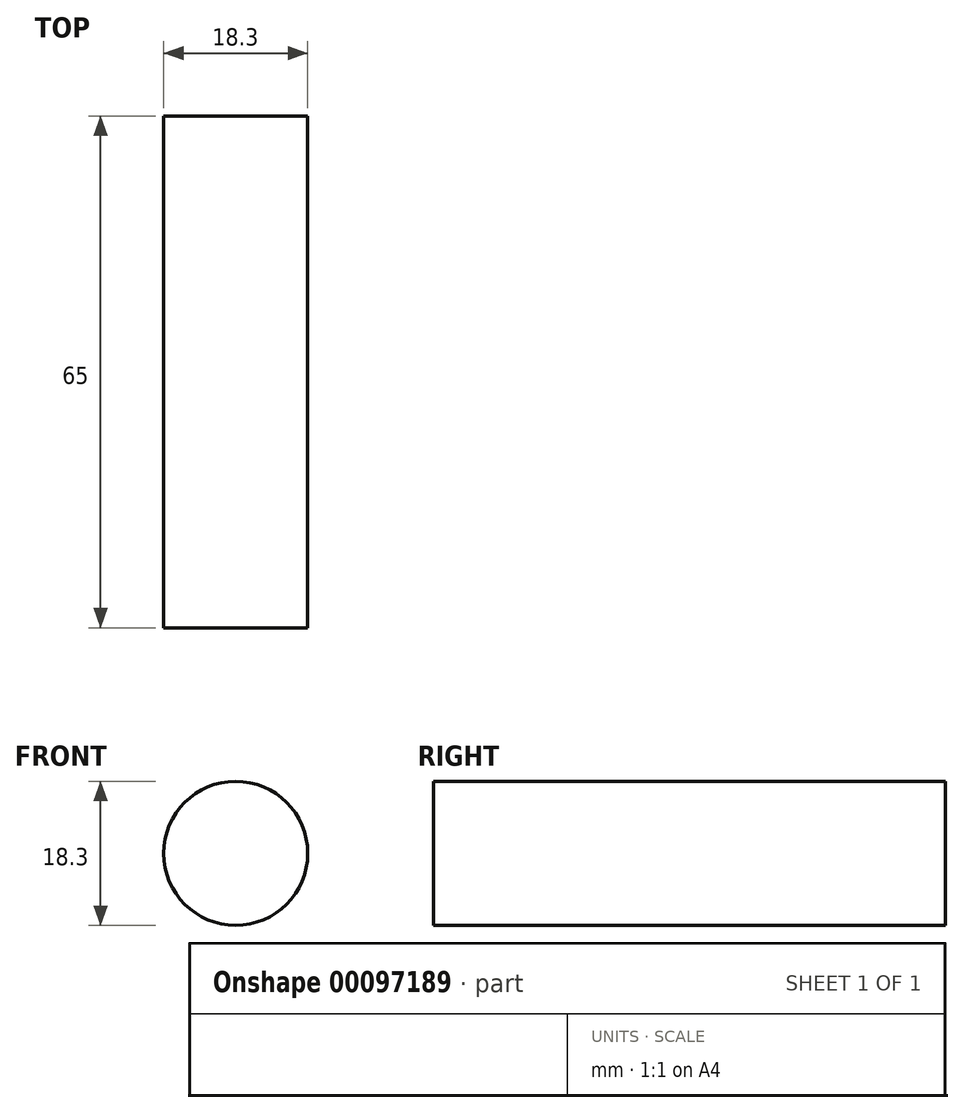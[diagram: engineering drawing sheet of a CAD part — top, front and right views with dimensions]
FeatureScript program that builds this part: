
annotation { "Feature Type Name" : "Feature", "Feature Type Description" : "" }
export const myFeature = defineFeature(function(context is Context, id is Id, definition is map)
    precondition{}
    {
        {
            var Q0;
            Q0=qCreatedBy(makeId("Front.planeOp"),FACE);
            var sketch = newSketch(context, id + "F0", { "sketchPlane" : qUnion([Q0])});
            skCircle(sketch, "E0", {"center": v(0, 0) * mm, "radius": 9.15 * mm});
            skSolve(sketch);
        }
        {
            var Q0;
            Q0=makeQuery(id+"F0.imprint","IMPRINT",FACE,{"disambiguationData":[TD([[makeQuery(id+"F0.imprint","IMPRINT",EDGE,{"derivedFrom":sQuery(id+"F0.wireOp",EDGE,"E0")}),1.0]])]});
            extrude(context, id + "F1", {"entities" : qUnion([Q0]), "endBound" : BoundingType.SYMMETRIC, "depth" : 65 * mm});
        }
    });
